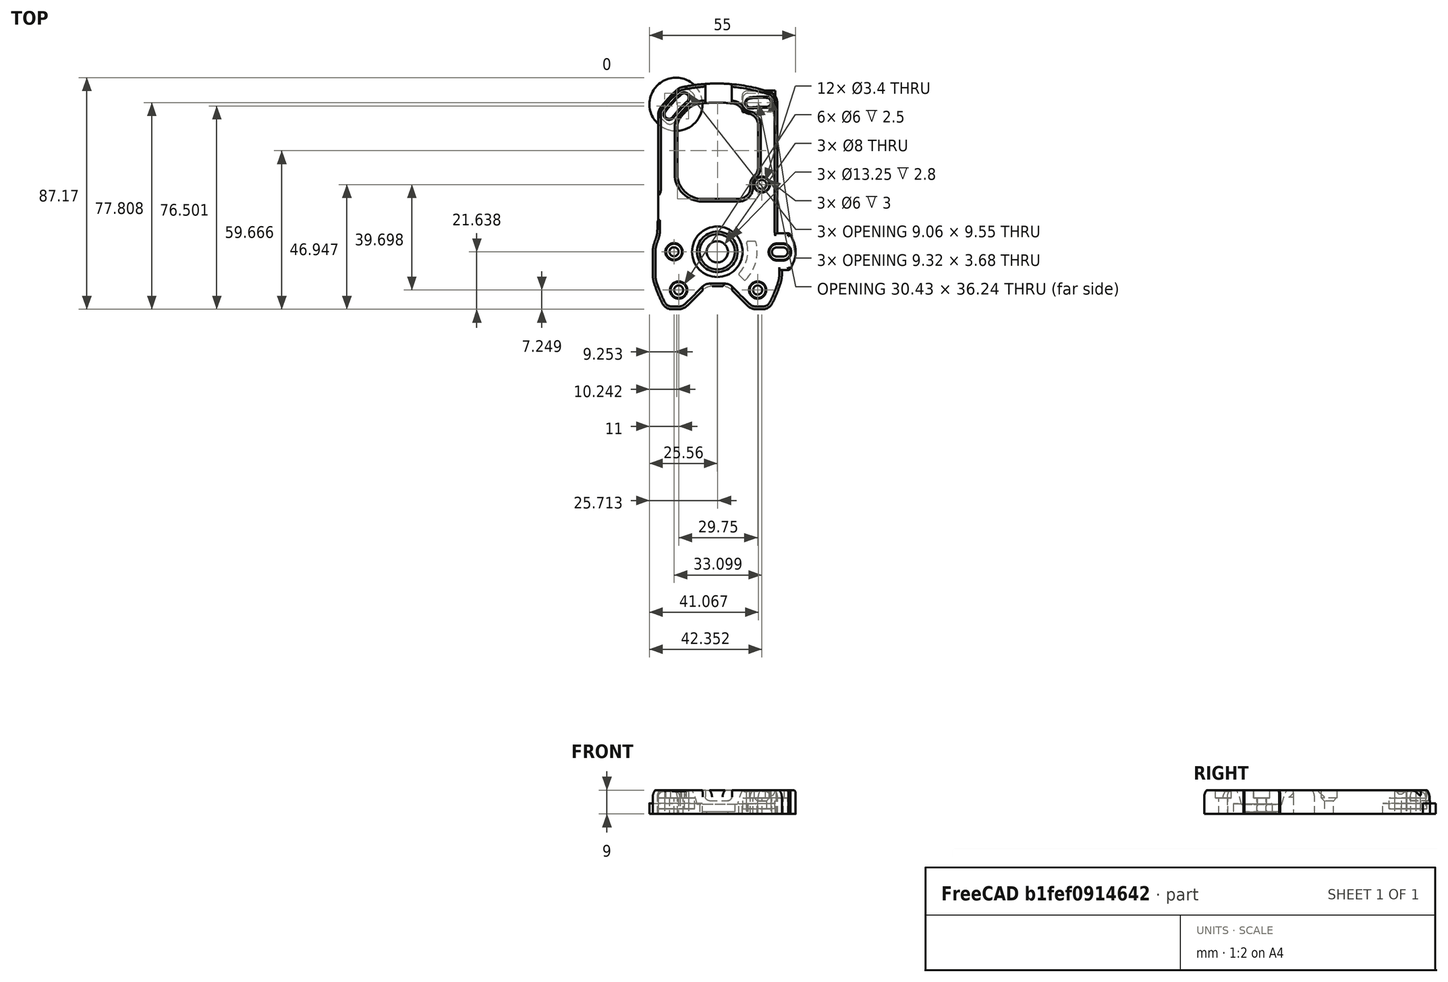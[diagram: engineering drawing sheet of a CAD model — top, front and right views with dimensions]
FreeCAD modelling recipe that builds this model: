
FCSTD DOCUMENT  (FreeCAD 0.18R16146 (Git))
Label: z-motor-mount
License: All rights reserved
LicenseURL: http://en.wikipedia.org/wiki/All_rights_reserved
objects: Part::Feature×6, Part::Box×3, Part::MultiFuse×3, Part::Fillet×2, Part::Cylinder×1, Part::MultiCommon×1
note: 16 computed .brp shape members not serialized (recipe doc carries the construction recipe); baked Part::Feature solids carry a one-line shape summary decoded from their .brp

FEATURE [Part::Feature] Part__Feature  label="V0-ZBelt-Pancake-Stepper-Bracket-ver1-Keyed-BETA1 (1)"
  Placement = pos=(53,121,-180.9) rot=(0,0.707107,0.707107;3.14159rad)
  shape: bbox 54.03 x 85.18 x 13.64 mm, 191 faces (baked)
FEATURE [Part::Cylinder] Cylinder
  Angle = 360
  AttacherType = Attacher::AttachEngine3D
  Height = 4
  Placement = pos=(-12,36,0) rot=(0,0,1;0rad)
  Radius = 10
FEATURE [Part::Feature] Part__Feature001  label="V0-ZBelt-Pancake-Stepper-Bracket-ver1-Keyed-BETA1 (1)001"
  Placement = pos=(53,121,-180.9) rot=(0,0.707107,0.707107;3.14159rad)
  shape: bbox 54.03 x 85.18 x 13.64 mm, 191 faces (baked)
FEATURE [Part::Box] Box  label="Cube"
  AttacherType = Attacher::AttachEngine3D
  Height = 4
  Length = 12.5
  Placement = pos=(13,33,0) rot=(0,0,1;0.017453rad)
  Width = 8
FEATURE [Part::MultiFuse] Fusion
  Shapes = -> [Box,Cylinder]
FEATURE [Part::Fillet] Fillet
  Base = -> Fusion
  Edges = 2 edges r=2: [Edge3,Edge5]
FEATURE [Part::Box] Box001  label="Cube001"
  AttacherType = Attacher::AttachEngine3D
  Height = 4
  Length = 15
  Placement = pos=(-14.1783,27.668,0) rot=(0,0,1;0.837758rad)
  Width = 7
FEATURE [Part::Box] Box002  label="Cube002"
  AttacherType = Attacher::AttachEngine3D
  Height = 4
  Length = 12
  Placement = pos=(13.3174,33.1003,0) rot=(0,0,1;0.034907rad)
  Width = 7
FEATURE [Part::MultiFuse] Fusion001
  Shapes = -> [Box001,Box002]
FEATURE [Part::Fillet] Fillet001
  Base = -> Fusion001
  Edges = 8 edges r=2: [Edge1,Edge3,Edge5,Edge7,Edge13,Edge15,Edge17,Edge19]
FEATURE [Part::MultiCommon] Common
  Placement = pos=(0,0,4) rot=(0,0,1;0rad)
  Shapes = -> [Part__Feature001,Fillet001]
FEATURE [Part::Feature] Common001
  Placement = pos=(0,0,2) rot=(0,0,1;0rad)
  shape: bbox 43.8 x 14.13 x 4 mm, 31 faces, 2 solids (baked)
FEATURE [Part::Feature] Common002
  Placement = pos=(0,0,5) rot=(0,0,1;0rad)
  shape: bbox 43.8 x 14.13 x 4 mm, 31 faces, 2 solids (baked)
FEATURE [Part::Feature] Part__Feature002  label="V0-ZBelt-Pancake-Stepper-Bracket-ver1-Keyed-BETA1 (1)002"
  Placement = pos=(53,121,-180.9) rot=(0,0.707107,0.707107;3.14159rad)
  shape: bbox 54.04 x 85.19 x 13.65 mm, 191 faces (baked)
FEATURE [Part::MultiFuse] Fusion002
  Shapes = -> [Part__Feature002,Common,Common002]
FEATURE [Part::Feature] Fusion002001  label="Fusion003"
  shape: bbox 54.04 x 85.19 x 13.65 mm, 203 faces (baked)
